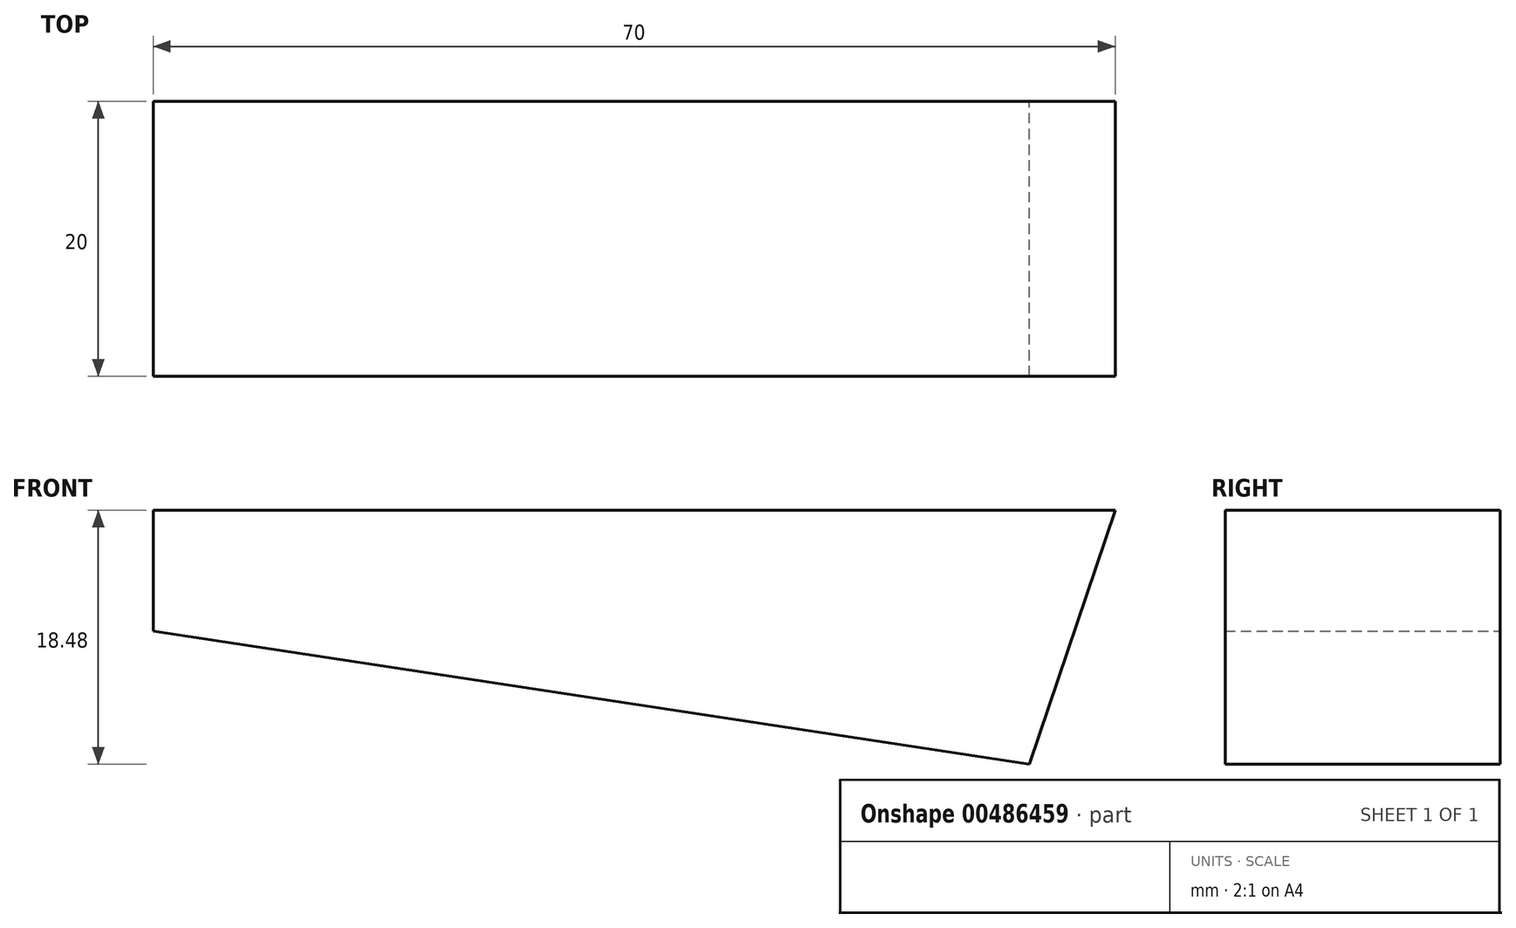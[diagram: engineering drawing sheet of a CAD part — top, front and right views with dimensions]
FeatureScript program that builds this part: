
annotation { "Feature Type Name" : "Feature", "Feature Type Description" : "" }
export const myFeature = defineFeature(function(context is Context, id is Id, definition is map)
    precondition{}
    {
        {
            var Q0;
            Q0=qCreatedBy(makeId("Front.planeOp"),FACE);
            var sketch = newSketch(context, id + "F0", { "sketchPlane" : qUnion([Q0])});
            skLineSegment(sketch, "E0", {"start": v(0, 0) * mm, "end": v(70, 0) * mm});
            skLineSegment(sketch, "E1", {"start": v(70, 0) * mm, "end": v(63.77, -18.48) * mm});
            skLineSegment(sketch, "E2", {"start": v(63.77, -18.48) * mm, "end": v(0, -8.8) * mm});
            skLineSegment(sketch, "E3", {"start": v(0, -8.8) * mm, "end": v(0, 0) * mm});
            skSolve(sketch);
        }
        {
            var Q0;
            Q0=makeQuery(id+"F0.imprint","IMPRINT",FACE,{"disambiguationData":[TD([[makeQuery(id+"F0.imprint","IMPRINT",EDGE,{"derivedFrom":sQuery(id+"F0.wireOp",EDGE,"E0")}),-1.0]])]});
            extrude(context, id + "F1", {"entities" : qUnion([Q0]), "endBound" : BoundingType.SYMMETRIC, "depth" : 20 * mm, "offsetDistance" : 25 * mm});
        }
    });
